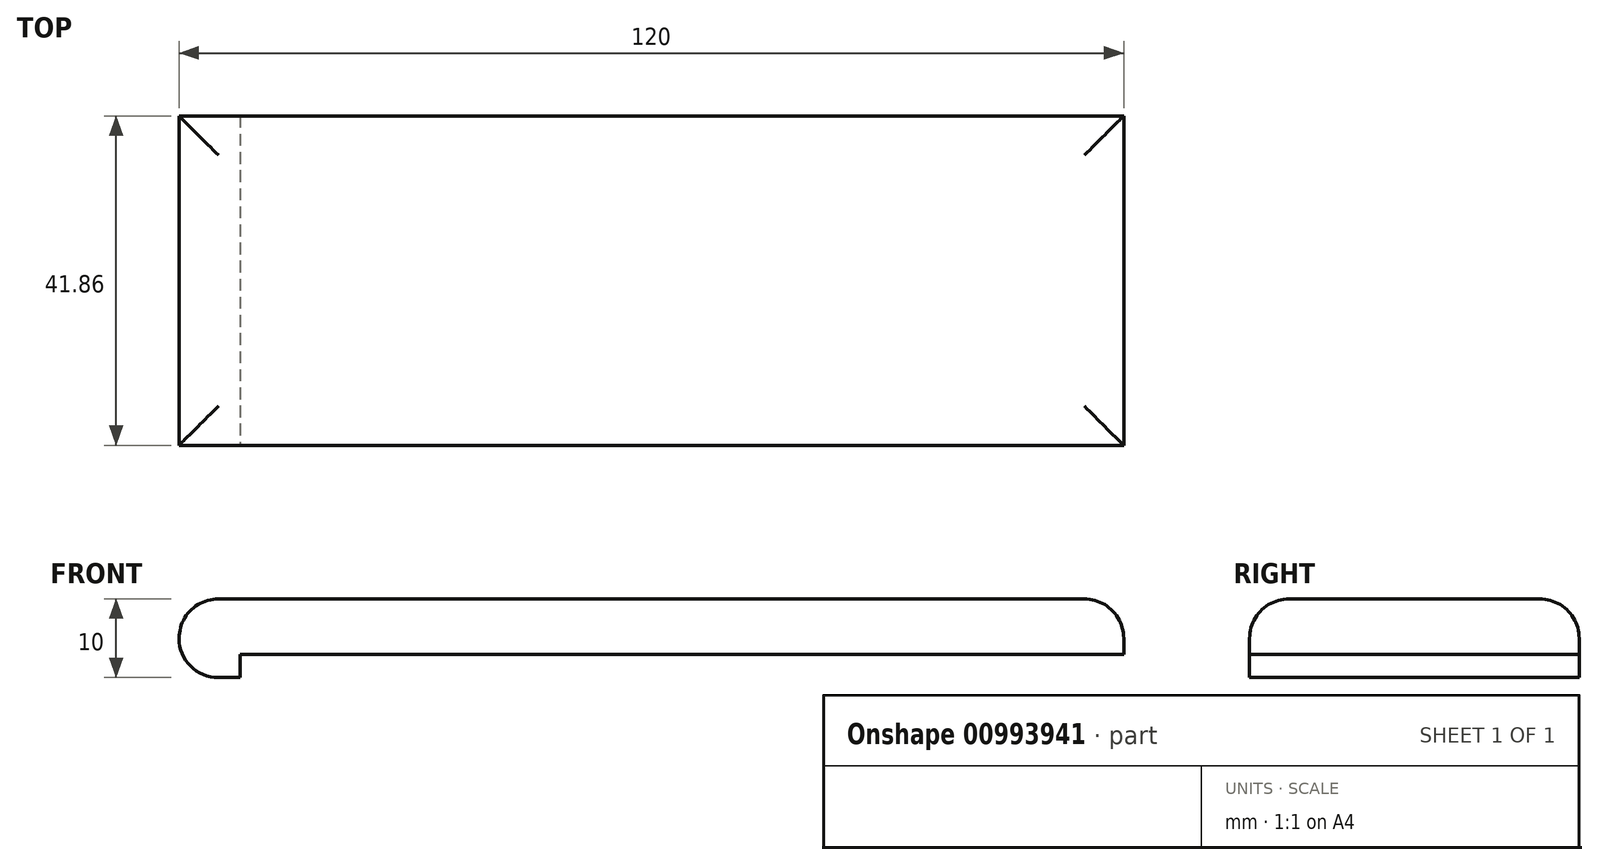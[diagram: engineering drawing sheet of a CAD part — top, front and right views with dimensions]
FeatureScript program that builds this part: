
annotation { "Feature Type Name" : "Feature", "Feature Type Description" : "" }
export const myFeature = defineFeature(function(context is Context, id is Id, definition is map)
    precondition{}
    {
        {
            var Q0;
            Q0=qCreatedBy(makeId("Top.planeOp"),FACE);
            var sketch = newSketch(context, id + "F0", { "sketchPlane" : qUnion([Q0])});
            skLineSegment(sketch, "E0.bottom", {"start": v(-64.22, 31.09) * mm, "end": v(55.78, 31.09) * mm});
            skLineSegment(sketch, "E0.top", {"start": v(-64.22, -10.77) * mm, "end": v(55.78, -10.77) * mm});
            skLineSegment(sketch, "E0.left", {"start": v(-64.22, 31.09) * mm, "end": v(-64.22, -10.77) * mm});
            skLineSegment(sketch, "E0.right", {"start": v(55.78, 31.09) * mm, "end": v(55.78, -10.77) * mm});
            skSolve(sketch);
        }
        {
            var Q0;
            Q0=makeQuery(id+"F0.imprint","IMPRINT",FACE,{"disambiguationData":[TD([[makeQuery(id+"F0.imprint","IMPRINT",EDGE,{"derivedFrom":sQuery(id+"F0.wireOp",EDGE,"E0.bottom")}),-1.0]])]});
            extrude(context, id + "F1", {"entities" : qUnion([Q0]), "depth" : 10 * mm, "offsetDistance" : 25 * mm});
        }
        {
            var Q0;
            Q0=makeQuery(id+"F1.opExtrude","SWEPT_FACE",FACE,{"disambiguationData":[OSD([sQuery(id+"F0.wireOp",EDGE,"E0.top")])]});
            var sketch = newSketch(context, id + "F2", { "sketchPlane" : qUnion([Q0])});
            skLineSegment(sketch, "E1.bottom", {"start": v(-56.45, 0) * mm, "end": v(55.78, 0) * mm});
            skLineSegment(sketch, "E1.top", {"start": v(-56.45, 2.95) * mm, "end": v(55.78, 2.95) * mm});
            skLineSegment(sketch, "E1.left", {"start": v(-56.45, 0) * mm, "end": v(-56.45, 2.95) * mm});
            skLineSegment(sketch, "E1.right", {"start": v(55.78, 0) * mm, "end": v(55.78, 2.95) * mm});
            skSolve(sketch);
        }
        {
            var Q0;
            Q0 = qSketchRegion(id + "F2", true);
            extrude(context, id + "F3", {"entities" : qUnion([Q0]), "operationType" : NewBodyOperationType.REMOVE, "oppositeDirection" : true, "depth" : 73.9 * mm, "offsetDistance" : 25 * mm});
        }
        {
            var Q0;
            Q0=makeQuery(id+"F1.opExtrude","CAP_EDGE",EDGE,{"disambiguationData":[OSD([sQuery(id+"F0.wireOp",EDGE,"E0.left")])],"isStart":false});
            var Q1;
            Q1=makeQuery(id+"F1.opExtrude","CAP_EDGE",EDGE,{"disambiguationData":[OSD([sQuery(id+"F0.wireOp",EDGE,"E0.bottom")])],"isStart":false});
            var Q2;
            Q2=makeQuery(id+"F1.opExtrude","CAP_EDGE",EDGE,{"disambiguationData":[OSD([sQuery(id+"F0.wireOp",EDGE,"E0.top")])],"isStart":false});
            var Q3;
            Q3=makeQuery(id+"F1.opExtrude","CAP_EDGE",EDGE,{"disambiguationData":[OSD([sQuery(id+"F0.wireOp",EDGE,"E0.right")])],"isStart":false});
            var Q4;
            Q4=makeQuery(id+"F1.opExtrude","CAP_EDGE",EDGE,{"disambiguationData":[OSD([sQuery(id+"F0.wireOp",EDGE,"E0.left")])],"isStart":true});
            fillet(context, id + "F4", {"entities" : qUnion([Q0, Q1, Q2, Q3, Q4]), "radius" : 5 * mm, "tangentPropagation" : true, "allowEdgeOverflow" : false});
        }
    });
